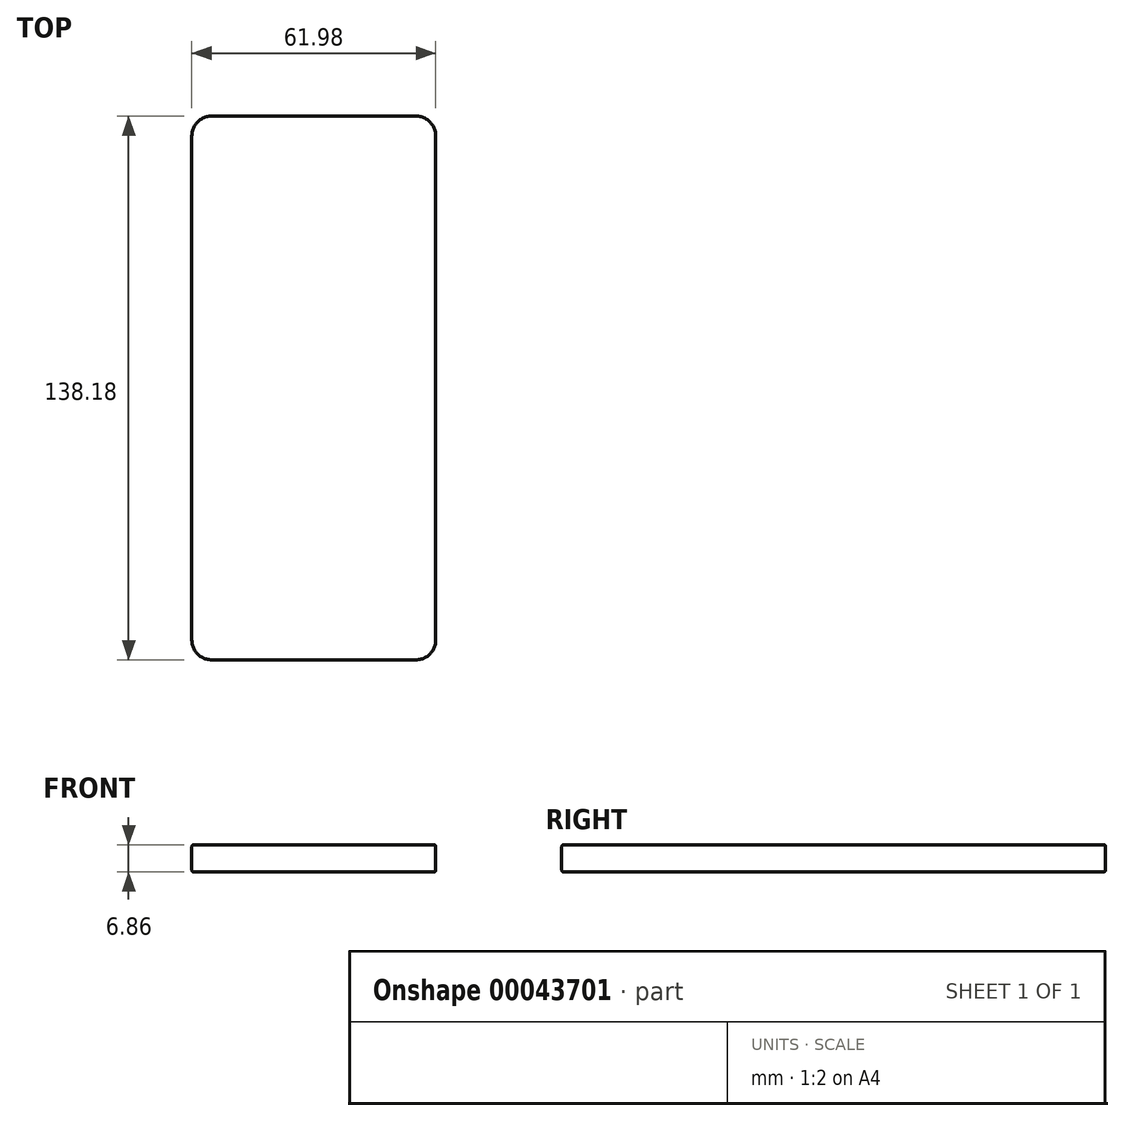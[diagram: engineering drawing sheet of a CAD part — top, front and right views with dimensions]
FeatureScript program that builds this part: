
annotation { "Feature Type Name" : "Feature", "Feature Type Description" : "" }
export const myFeature = defineFeature(function(context is Context, id is Id, definition is map)
    precondition{}
    {
        {
            var Q0;
            Q0=qCreatedBy(makeId("Top.planeOp"),FACE);
            var sketch = newSketch(context, id + "F0", { "sketchPlane" : qUnion([Q0])});
            skLineSegment(sketch, "E0.rect.bottom", {"start": v(30.99, 69.09) * mm, "end": v(-30.99, 69.09) * mm});
            skLineSegment(sketch, "E0.rect.top", {"start": v(30.99, -69.09) * mm, "end": v(-30.99, -69.09) * mm});
            skLineSegment(sketch, "E0.rect.left", {"start": v(-30.99, 69.09) * mm, "end": v(-30.99, -69.09) * mm});
            skLineSegment(sketch, "E0.rect.right", {"start": v(30.99, 69.09) * mm, "end": v(30.99, -69.09) * mm});
            skPoint(sketch, "E0.rect.middle", {"position": v(0, 0) * mm});
            skSolve(sketch);
        }
        {
            var Q0;
            Q0=makeQuery(id+"F0.imprint","IMPRINT",FACE,{"disambiguationData":[TD([[makeQuery(id+"F0.imprint","IMPRINT",EDGE,{"derivedFrom":sQuery(id+"F0.wireOp",EDGE,"E0.rect.bottom")}),1.0]])]});
            var Q1;
            Q1=sQuery(id+"F0.wireOp",EDGE,"E0.rect.right");
            var Q2;
            Q2=sQuery(id+"F0.wireOp",EDGE,"E0.rect.top");
            var Q3;
            Q3=sQuery(id+"F0.wireOp",EDGE,"E0.rect.bottom");
            var Q4;
            Q4=sQuery(id+"F0.wireOp",EDGE,"E0.rect.left");
            extrude(context, id + "F1", {"entities" : qUnion([Q0]), "surfaceEntities" : qUnion([Q1, Q2, Q3, Q4]), "depth" : 6.86 * mm});
        }
        {
            var Q0;
            Q0=makeQuery(id+"F1.opExtrude","SWEPT_EDGE",EDGE,{"disambiguationData":[OSD([sQuery(id+"F0.wireOp",EDGE,"E0.rect.bottom"),sQuery(id+"F0.wireOp",EDGE,"E0.rect.right")])]});
            var Q1;
            Q1=makeQuery(id+"F1.opExtrude","SWEPT_EDGE",EDGE,{"disambiguationData":[OSD([sQuery(id+"F0.wireOp",EDGE,"E0.rect.top"),sQuery(id+"F0.wireOp",EDGE,"E0.rect.right")])]});
            var Q2;
            Q2=makeQuery(id+"F1.opExtrude","SWEPT_EDGE",EDGE,{"disambiguationData":[OSD([sQuery(id+"F0.wireOp",EDGE,"E0.rect.bottom"),sQuery(id+"F0.wireOp",EDGE,"E0.rect.left")])]});
            var Q3;
            Q3=makeQuery(id+"F1.opExtrude","SWEPT_EDGE",EDGE,{"disambiguationData":[OSD([sQuery(id+"F0.wireOp",EDGE,"E0.rect.top"),sQuery(id+"F0.wireOp",EDGE,"E0.rect.left")])]});
            fillet(context, id + "F2", {"entities" : qUnion([Q0, Q1, Q2, Q3]), "radius" : 5.08 * mm, "tangentPropagation" : true, "allowEdgeOverflow" : false});
        }
        {
            var Q0;
            Q0=makeQuery(id+"F1.opExtrude","CAP_EDGE",EDGE,{"disambiguationData":[OSD([sQuery(id+"F0.wireOp",EDGE,"E0.rect.left")])],"isStart":false});
            var Q1;
            Q1=makeQuery(id+"F1.opExtrude","CAP_EDGE",EDGE,{"disambiguationData":[OSD([sQuery(id+"F0.wireOp",EDGE,"E0.rect.bottom")])],"isStart":false});
            var Q2;
            {var subQ0=sQuery(id+"F0.wireOp",EDGE,"E0.rect.bottom");var subQ1=sQuery(id+"F0.wireOp",EDGE,"E0.rect.right");Q2=makeQuery(id+"F2.opFillet","BLEND_EDGE",EDGE,{"blendedFrom":[makeQuery(id+"F1.opExtrude","SWEPT_EDGE",EDGE,{"disambiguationData":[OSD([subQ0,subQ1])]}),makeQuery(id+"F1.opExtrude","CAP_FACE",FACE,{"disambiguationData":[OSD([subQ0,sQuery(id+"F0.wireOp",EDGE,"E0.rect.top"),sQuery(id+"F0.wireOp",EDGE,"E0.rect.left"),subQ1])],"isStart":true})],"blendedInto":[makeQuery(id+"F1.opExtrude","CAP_FACE",FACE,{"disambiguationData":[OSD([subQ0,sQuery(id+"F0.wireOp",EDGE,"E0.rect.top"),sQuery(id+"F0.wireOp",EDGE,"E0.rect.left"),subQ1])],"isStart":true})]});}
            var Q3;
            {var subQ0=sQuery(id+"F0.wireOp",EDGE,"E0.rect.bottom");var subQ1=sQuery(id+"F0.wireOp",EDGE,"E0.rect.left");Q3=makeQuery(id+"F2.opFillet","BLEND_EDGE",EDGE,{"blendedFrom":[makeQuery(id+"F1.opExtrude","SWEPT_EDGE",EDGE,{"disambiguationData":[OSD([subQ0,subQ1])]}),makeQuery(id+"F1.opExtrude","CAP_FACE",FACE,{"disambiguationData":[OSD([subQ0,sQuery(id+"F0.wireOp",EDGE,"E0.rect.top"),subQ1,sQuery(id+"F0.wireOp",EDGE,"E0.rect.right")])],"isStart":true})],"blendedInto":[makeQuery(id+"F1.opExtrude","CAP_FACE",FACE,{"disambiguationData":[OSD([subQ0,sQuery(id+"F0.wireOp",EDGE,"E0.rect.top"),subQ1,sQuery(id+"F0.wireOp",EDGE,"E0.rect.right")])],"isStart":true})]});}
            var Q4;
            {var subQ0=sQuery(id+"F0.wireOp",EDGE,"E0.rect.top");var subQ1=sQuery(id+"F0.wireOp",EDGE,"E0.rect.right");Q4=makeQuery(id+"F2.opFillet","BLEND_EDGE",EDGE,{"blendedFrom":[makeQuery(id+"F1.opExtrude","SWEPT_EDGE",EDGE,{"disambiguationData":[OSD([subQ0,subQ1])]}),makeQuery(id+"F1.opExtrude","CAP_FACE",FACE,{"disambiguationData":[OSD([sQuery(id+"F0.wireOp",EDGE,"E0.rect.bottom"),subQ0,sQuery(id+"F0.wireOp",EDGE,"E0.rect.left"),subQ1])],"isStart":true})],"blendedInto":[makeQuery(id+"F1.opExtrude","CAP_FACE",FACE,{"disambiguationData":[OSD([sQuery(id+"F0.wireOp",EDGE,"E0.rect.bottom"),subQ0,sQuery(id+"F0.wireOp",EDGE,"E0.rect.left"),subQ1])],"isStart":true})]});}
            var Q5;
            {var subQ0=sQuery(id+"F0.wireOp",EDGE,"E0.rect.top");var subQ1=sQuery(id+"F0.wireOp",EDGE,"E0.rect.left");Q5=makeQuery(id+"F2.opFillet","BLEND_EDGE",EDGE,{"blendedFrom":[makeQuery(id+"F1.opExtrude","SWEPT_EDGE",EDGE,{"disambiguationData":[OSD([subQ0,subQ1])]}),makeQuery(id+"F1.opExtrude","CAP_FACE",FACE,{"disambiguationData":[OSD([sQuery(id+"F0.wireOp",EDGE,"E0.rect.bottom"),subQ0,subQ1,sQuery(id+"F0.wireOp",EDGE,"E0.rect.right")])],"isStart":false})],"blendedInto":[makeQuery(id+"F1.opExtrude","CAP_FACE",FACE,{"disambiguationData":[OSD([sQuery(id+"F0.wireOp",EDGE,"E0.rect.bottom"),subQ0,subQ1,sQuery(id+"F0.wireOp",EDGE,"E0.rect.right")])],"isStart":false})]});}
            var Q6;
            {var subQ0=sQuery(id+"F0.wireOp",EDGE,"E0.rect.bottom");var subQ1=sQuery(id+"F0.wireOp",EDGE,"E0.rect.left");Q6=makeQuery(id+"F2.opFillet","BLEND_EDGE",EDGE,{"blendedFrom":[makeQuery(id+"F1.opExtrude","SWEPT_EDGE",EDGE,{"disambiguationData":[OSD([subQ0,subQ1])]}),makeQuery(id+"F1.opExtrude","CAP_FACE",FACE,{"disambiguationData":[OSD([subQ0,sQuery(id+"F0.wireOp",EDGE,"E0.rect.top"),subQ1,sQuery(id+"F0.wireOp",EDGE,"E0.rect.right")])],"isStart":false})],"blendedInto":[makeQuery(id+"F1.opExtrude","CAP_FACE",FACE,{"disambiguationData":[OSD([subQ0,sQuery(id+"F0.wireOp",EDGE,"E0.rect.top"),subQ1,sQuery(id+"F0.wireOp",EDGE,"E0.rect.right")])],"isStart":false})]});}
            var Q7;
            Q7=makeQuery(id+"F1.opExtrude","CAP_EDGE",EDGE,{"disambiguationData":[OSD([sQuery(id+"F0.wireOp",EDGE,"E0.rect.right")])],"isStart":false});
            var Q8;
            Q8=makeQuery(id+"F1.opExtrude","CAP_EDGE",EDGE,{"disambiguationData":[OSD([sQuery(id+"F0.wireOp",EDGE,"E0.rect.bottom")])],"isStart":true});
            var Q9;
            {var subQ0=sQuery(id+"F0.wireOp",EDGE,"E0.rect.bottom");var subQ1=sQuery(id+"F0.wireOp",EDGE,"E0.rect.right");Q9=makeQuery(id+"F2.opFillet","BLEND_EDGE",EDGE,{"blendedFrom":[makeQuery(id+"F1.opExtrude","SWEPT_EDGE",EDGE,{"disambiguationData":[OSD([subQ0,subQ1])]}),makeQuery(id+"F1.opExtrude","CAP_FACE",FACE,{"disambiguationData":[OSD([subQ0,sQuery(id+"F0.wireOp",EDGE,"E0.rect.top"),sQuery(id+"F0.wireOp",EDGE,"E0.rect.left"),subQ1])],"isStart":false})],"blendedInto":[makeQuery(id+"F1.opExtrude","CAP_FACE",FACE,{"disambiguationData":[OSD([subQ0,sQuery(id+"F0.wireOp",EDGE,"E0.rect.top"),sQuery(id+"F0.wireOp",EDGE,"E0.rect.left"),subQ1])],"isStart":false})]});}
            var Q10;
            Q10=makeQuery(id+"F1.opExtrude","CAP_EDGE",EDGE,{"disambiguationData":[OSD([sQuery(id+"F0.wireOp",EDGE,"E0.rect.top")])],"isStart":true});
            var Q11;
            Q11=makeQuery(id+"F1.opExtrude","CAP_EDGE",EDGE,{"disambiguationData":[OSD([sQuery(id+"F0.wireOp",EDGE,"E0.rect.left")])],"isStart":true});
            var Q12;
            {var subQ0=sQuery(id+"F0.wireOp",EDGE,"E0.rect.top");var subQ1=sQuery(id+"F0.wireOp",EDGE,"E0.rect.left");Q12=makeQuery(id+"F2.opFillet","BLEND_EDGE",EDGE,{"blendedFrom":[makeQuery(id+"F1.opExtrude","SWEPT_EDGE",EDGE,{"disambiguationData":[OSD([subQ0,subQ1])]}),makeQuery(id+"F1.opExtrude","CAP_FACE",FACE,{"disambiguationData":[OSD([sQuery(id+"F0.wireOp",EDGE,"E0.rect.bottom"),subQ0,subQ1,sQuery(id+"F0.wireOp",EDGE,"E0.rect.right")])],"isStart":true})],"blendedInto":[makeQuery(id+"F1.opExtrude","CAP_FACE",FACE,{"disambiguationData":[OSD([sQuery(id+"F0.wireOp",EDGE,"E0.rect.bottom"),subQ0,subQ1,sQuery(id+"F0.wireOp",EDGE,"E0.rect.right")])],"isStart":true})]});}
            var Q13;
            {var subQ0=sQuery(id+"F0.wireOp",EDGE,"E0.rect.top");var subQ1=sQuery(id+"F0.wireOp",EDGE,"E0.rect.right");Q13=makeQuery(id+"F2.opFillet","BLEND_EDGE",EDGE,{"blendedFrom":[makeQuery(id+"F1.opExtrude","SWEPT_EDGE",EDGE,{"disambiguationData":[OSD([subQ0,subQ1])]}),makeQuery(id+"F1.opExtrude","CAP_FACE",FACE,{"disambiguationData":[OSD([sQuery(id+"F0.wireOp",EDGE,"E0.rect.bottom"),subQ0,sQuery(id+"F0.wireOp",EDGE,"E0.rect.left"),subQ1])],"isStart":false})],"blendedInto":[makeQuery(id+"F1.opExtrude","CAP_FACE",FACE,{"disambiguationData":[OSD([sQuery(id+"F0.wireOp",EDGE,"E0.rect.bottom"),subQ0,sQuery(id+"F0.wireOp",EDGE,"E0.rect.left"),subQ1])],"isStart":false})]});}
            var Q14;
            Q14=makeQuery(id+"F1.opExtrude","CAP_EDGE",EDGE,{"disambiguationData":[OSD([sQuery(id+"F0.wireOp",EDGE,"E0.rect.right")])],"isStart":true});
            var Q15;
            Q15=makeQuery(id+"F1.opExtrude","CAP_EDGE",EDGE,{"disambiguationData":[OSD([sQuery(id+"F0.wireOp",EDGE,"E0.rect.top")])],"isStart":false});
            fillet(context, id + "F3", {"entities" : qUnion([Q0, Q1, Q2, Q3, Q4, Q5, Q6, Q7, Q8, Q9, Q10, Q11, Q12, Q13, Q14, Q15]), "radius" : 0.5 * mm, "tangentPropagation" : true, "rho" : 0.5, "crossSection" : FilletCrossSection.CONIC, "allowEdgeOverflow" : false});
        }
    });
